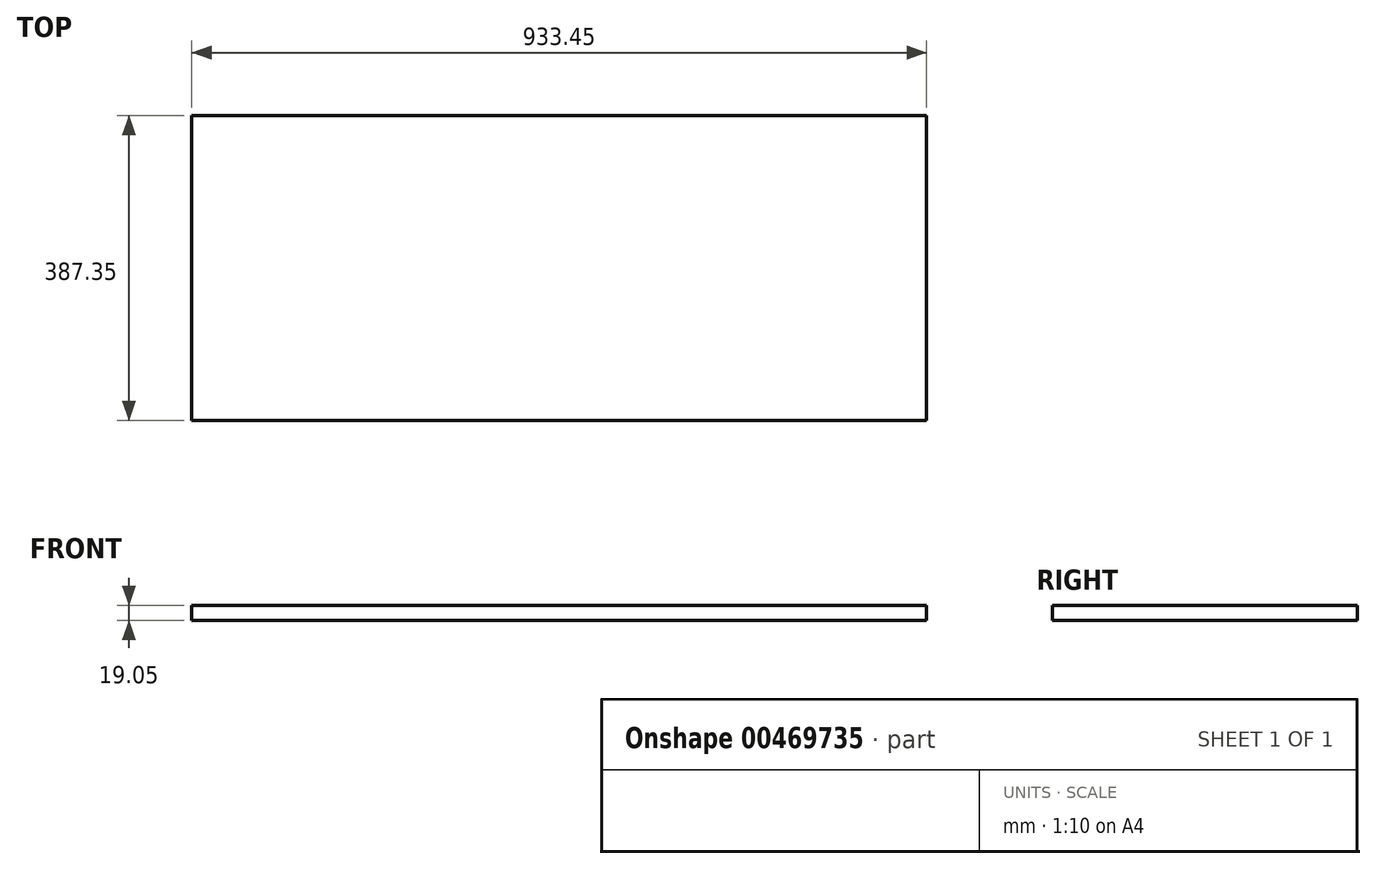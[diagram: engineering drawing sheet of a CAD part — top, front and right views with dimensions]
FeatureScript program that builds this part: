
annotation { "Feature Type Name" : "Feature", "Feature Type Description" : "" }
export const myFeature = defineFeature(function(context is Context, id is Id, definition is map)
    precondition{}
    {
        {
            var Q0;
            Q0=qCreatedBy(makeId("Front.planeOp"),FACE);
            var sketch = newSketch(context, id + "F0", { "sketchPlane" : qUnion([Q0])});
            skLineSegment(sketch, "E0.bottom", {"start": v(0, 0) * mm, "end": v(933.45, 0) * mm});
            skLineSegment(sketch, "E0.top", {"start": v(0, 19.05) * mm, "end": v(933.45, 19.05) * mm});
            skLineSegment(sketch, "E0.left", {"start": v(0, 0) * mm, "end": v(0, 19.05) * mm});
            skLineSegment(sketch, "E0.right", {"start": v(933.45, 0) * mm, "end": v(933.45, 19.05) * mm});
            skSolve(sketch);
        }
        {
            var Q0;
            Q0=makeQuery(id+"F0.imprint","IMPRINT",FACE,{"disambiguationData":[TD([[makeQuery(id+"F0.imprint","IMPRINT",EDGE,{"derivedFrom":sQuery(id+"F0.wireOp",EDGE,"E0.bottom")}),1.0]])]});
            extrude(context, id + "F1", {"entities" : qUnion([Q0]), "depth" : 387.35 * mm, "offsetDistance" : 25.4 * mm});
        }
    });
